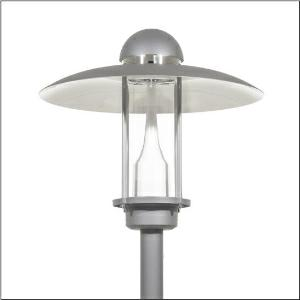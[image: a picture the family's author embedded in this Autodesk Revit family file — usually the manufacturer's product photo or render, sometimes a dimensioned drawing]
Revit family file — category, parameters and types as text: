
# Revit family: city-light_elegance_iq___pl1_2s_5xa5265cf14h_c70b
name_source: partatom
category: Lighting Fixtures
units: mm (PartAtom-declared; Revit-internal decimal feet)

## family parameters
Cut with Voids When Loaded = No
Host = Face
Light Source = No
Part Type = Normal
Room Calculation Point = No
Round Connector Dimension = Use Diameter
Shared = No

## types (1)
- --- (1 x LED, 2840 lm, 23.9 W, 2200K)
    Apparent Load = 24 VA
    CIE Flux Codes = 24 63 94 98 100
    Color Rendering = 70
    Color Temperature = 2200K
    Default Elevation = 1800 mm
    Description = City-Light Elegance iQ, mast luminaire, Module 540 iQ-SR, primary light control with 3 zone facetted reflector, of plastic, silver coated, highly specular, structured, primary optical cover: cover, of PMMA, transparent, light distribution: PL1.2s, light emission: direct distribution, primary light characteristic: symmetric, installation type: post-top, LED, High Power LED, rated luminous flux: 2.840lm, luminous efficacy: 119lm/W, light colour: 722, colour temperature: 2200K, control gear: ECG iQ, control: pre-setting: logarithmic dimming characteristic, Street-Remote, Auto-Match, Temp-Guard, Lumen-Switch, Night-Set, Smart-Wire, Light-Fading, Desk-Remote (wireless, voltage-free reading and setting of iQ features in the workshop via application-optimized NFC function/RFID function), optimised constant luminous flux control (CLO 2.0), with terminal, 6-pole, max. 2.5mm², mains connection: 230..240V, AC, 50/60Hz, start of lifetime: 24W, end of service life: 26W, reduction: 12W, luminaire housing, upper part, of aluminium, coated, Siteco® metallic grey (DB 702S), diameter: 750mm, height: 675mm, spigot size: d x l = 76 x 70mm (post-top) | with reducer (optional accessory) 60 x 70mm, post-top mast mounting element, of diecast aluminium, coated, Siteco® metallic grey (DB 702S), Module 540 iQ-SR, traffic white (RAL 9016), equipment: standard, protection rating (complete): IP65, insulation class (complete): insulation class II (safety insulation), certification: CE, ENEC, VDE, packaging unit: 1 piece

Light Distribution: PL1.2s
    Height = 675 mm
    Lamp = 1 x LED
    Lamp Light Flux = 2840 lm
    Lamp Power = 23.9 W
    Lamp count = 1
    Length = 750 mm
    Luminous efficacy = 119 lm/W
    Manufacturer = Siteco
    ModVariant = No
    Model = 5XA5265CF14H
    Number of Poles = 1
    OnlyDefault = Yes
    Power Factor = 1
    Product Name = City-Light Elegance iQ | PL1.2s
    Product group = mast luminaire | pylon top
    ProductGroupID = 6100
    Protection Class = Protection class II
    Protection Degree = IP 65
    RLX_Detail_Level = 1
    RLX_Emergency_Light_Flux = 0 lm
    RLX_Emergency_Type = 0
    RLX_Emergency_Type_DB = No
    RlxData = <blob elided: 72721 chars, md5=a8b95751>
    Socket = socket
    Standby Power = 0 W
    System Light Flux = 2840 lm
    System Power = 24 W
    Type Comments = factory setting: luminous flux: 100 % | dim-lin: 254 | 499 mA
    Type Image = l_1006912.jpg
    URL = http://relux.com
    VarID = @adj_115341
    Voltage = 0 V
    Weight = 0.00 kg
    Width = 0 mm  [stored 0 ft]

note: [stored X ft] marks values corroborated as IEEE doubles in the binary element streams (Revit-internal decimal feet)

## geometry (parser evidence)
native form markers: Blend x4, Sweep x10
no freeform markers — native parametric forms only
